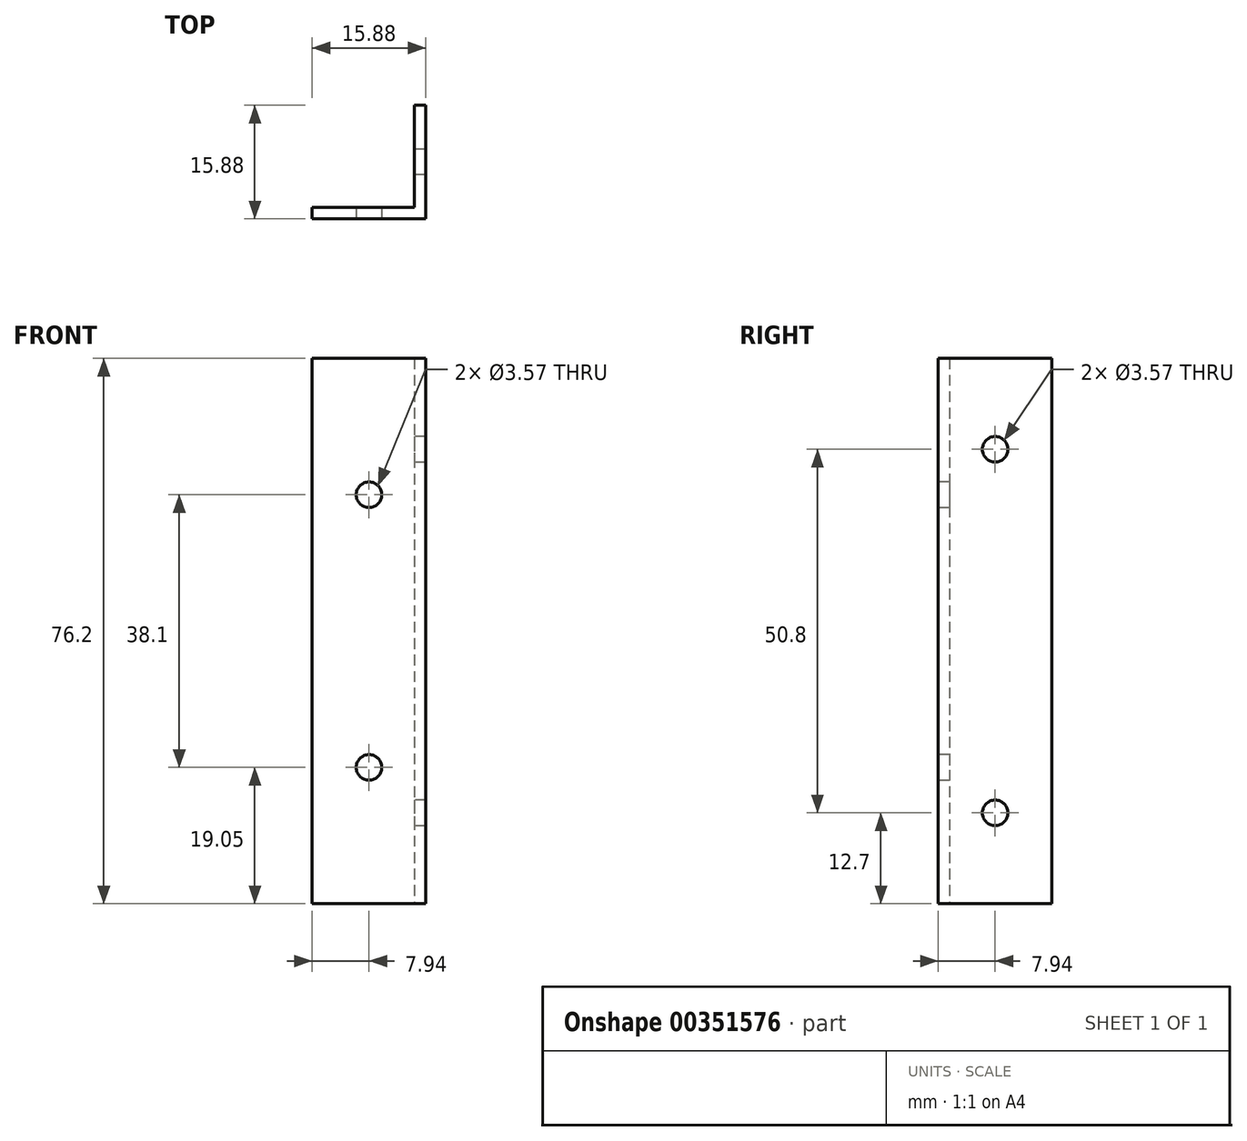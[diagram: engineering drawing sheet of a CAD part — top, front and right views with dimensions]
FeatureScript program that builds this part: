
annotation { "Feature Type Name" : "Feature", "Feature Type Description" : "" }
export const myFeature = defineFeature(function(context is Context, id is Id, definition is map)
    precondition{}
    {
        {
            var Q0;
            Q0=qCreatedBy(makeId("Top.planeOp"),FACE);
            var sketch = newSketch(context, id + "F0", { "sketchPlane" : qUnion([Q0])});
            skLineSegment(sketch, "E0.bottom", {"start": v(7.94, -7.94) * mm, "end": v(-7.94, -7.94) * mm});
            skLineSegment(sketch, "E0.top", {"start": v(7.94, 7.94) * mm, "end": v(6.35, 7.94) * mm});
            skLineSegment(sketch, "E0.left", {"start": v(7.94, -7.94) * mm, "end": v(7.94, 7.94) * mm});
            skLineSegment(sketch, "E0.right", {"start": v(-7.94, -7.94) * mm, "end": v(-7.94, -6.35) * mm});
            skPoint(sketch, "E0.middle", {"position": v(0, 0) * mm});
            skLineSegment(sketch, "E1", {"start": v(-7.94, -6.35) * mm, "end": v(6.35, -6.35) * mm});
            skLineSegment(sketch, "E2", {"start": v(6.35, 7.94) * mm, "end": v(6.35, -6.35) * mm});
            skPoint(sketch, "E3.orphan", {"position": v(-7.94, 7.94) * mm});
            skSolve(sketch);
        }
        {
            var Q0;
            Q0 = qSketchRegion(id + "F0", true);
            extrude(context, id + "F1", {"entities" : qUnion([Q0]), "depth" : 76.2 * mm, "symmetric" : true});
        }
        {
            var Q0;
            Q0=makeQuery(id+"F1.opExtrude","SWEPT_FACE",FACE,{"disambiguationData":[OSD([sQuery(id+"F0.wireOp",EDGE,"E2")])]});
            var sketch = newSketch(context, id + "F2", { "sketchPlane" : qUnion([Q0])});
            skCircle(sketch, "E4", {"center": v(0, -25.4) * mm, "radius": 1.79 * mm});
            skCircle(sketch, "E5.MirrorC", {"center": v(0, 25.4) * mm, "radius": 1.79 * mm});
            skSolve(sketch);
        }
        {
            var Q0;
            Q0 = qSketchRegion(id + "F2", true);
            var Q1;
            Q1=makeQuery(id+"F1.opExtrude","SWEPT_FACE",FACE,{"disambiguationData":[OSD([sQuery(id+"F0.wireOp",EDGE,"E0.left")])]});
            extrude(context, id + "F3", {"entities" : qUnion([Q0]), "operationType" : NewBodyOperationType.REMOVE, "endBound" : BoundingType.UP_TO_SURFACE, "oppositeDirection" : true, "endBoundEntityFace" : qUnion([Q1]), "depth" : 25.4 * mm});
        }
        {
            var Q0;
            Q0=makeQuery(id+"F1.opExtrude","SWEPT_FACE",FACE,{"disambiguationData":[OSD([sQuery(id+"F0.wireOp",EDGE,"E0.bottom")])]});
            var sketch = newSketch(context, id + "F4", { "sketchPlane" : qUnion([Q0])});
            skCircle(sketch, "E6", {"center": v(0, 19.05) * mm, "radius": 1.79 * mm});
            skCircle(sketch, "E7.MirrorC", {"center": v(0, -19.05) * mm, "radius": 1.79 * mm});
            skSolve(sketch);
        }
        {
            var Q0;
            Q0 = qSketchRegion(id + "F4", true);
            var Q1;
            Q1=makeQuery(id+"F1.opExtrude","SWEPT_FACE",FACE,{"disambiguationData":[OSD([sQuery(id+"F0.wireOp",EDGE,"E1")])]});
            extrude(context, id + "F5", {"entities" : qUnion([Q0]), "operationType" : NewBodyOperationType.REMOVE, "endBound" : BoundingType.UP_TO_SURFACE, "oppositeDirection" : true, "endBoundEntityFace" : qUnion([Q1]), "depth" : 25.4 * mm});
        }
    });
